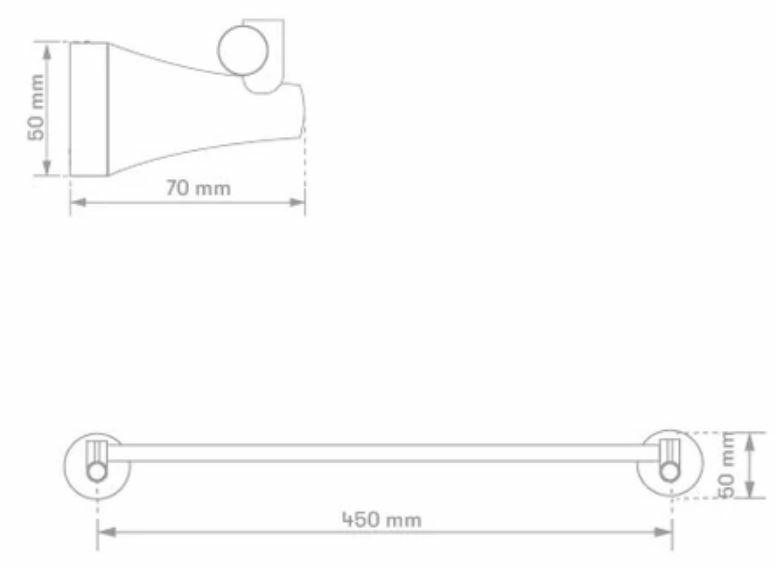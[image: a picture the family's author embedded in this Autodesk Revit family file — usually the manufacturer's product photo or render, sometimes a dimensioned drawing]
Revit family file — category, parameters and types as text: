
# Revit family: BL-2507-11 TOALLERO BARRA CONTEMPRA
name_source: partatom
category: Plumbing Fixtures
revit_build: Autodesk Revit 2018 (Build: 20170223_1515(x64)
units: mm (PartAtom-declared; Revit-internal decimal feet)

## family parameters
Cut with Voids When Loaded = No
Host = Face
OmniClass Number = 23.31.11.00
Part Type = Normal
Room Calculation Point = No
Round Connector Dimension = Use Diameter
Shared = No

## types (1)
- BL-2507-11
    Alto soporte = 70 mm
    Ancho = 450 mm
    CW Connection = Yes
    Default Elevation = 0 mm  [stored 0 ft]
    Description = Toallero
    Diametro base = 50 mm  [stored 0.164042 ft]
    HW Connection = Yes
    Link Ficha Tecnica = http://infotecnica.gricol.com
    Manufacturer = Gricol
    Model = BL-2507-11
    Plastico ABS cromado = Plastico - ABS Cromado
    Product Name = TOALLERO BARRA CONTEMPRA
    Type Image = <None>
    URL = https://www.gricol.com
    Vent Connection = No
    Waste Connection = No

note: [stored X ft] marks values corroborated as IEEE doubles in the binary element streams (Revit-internal decimal feet)

## geometry (parser evidence)
native form markers: Blend x2, Sweep x4
no freeform markers — native parametric forms only
